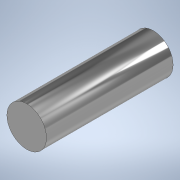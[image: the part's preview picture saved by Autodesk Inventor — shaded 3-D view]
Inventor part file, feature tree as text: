
AUTODESK INVENTOR PART (.ipt)
format: ipt  version: 2021 (Build 250183000, 183)  size: 97,792 bytes
history: native  units: mm
features: other x1, extrude x1, sketch x1
ambient origin geometry x8: Origin, YZ Plane, XZ Plane, XY Plane, X Axis, Y Axis, Z Axis, Center Point
bodies: Body1 (feature_tree)
feature tree (3):
  other  "Sólido1"
  extrude  "Extrusão1"  Depth=1.6mm TaperAngle=0.0deg
  sketch  "Esboço1"  dims[d0=0.5mm d1=1.6mm d2=0.0mm]
